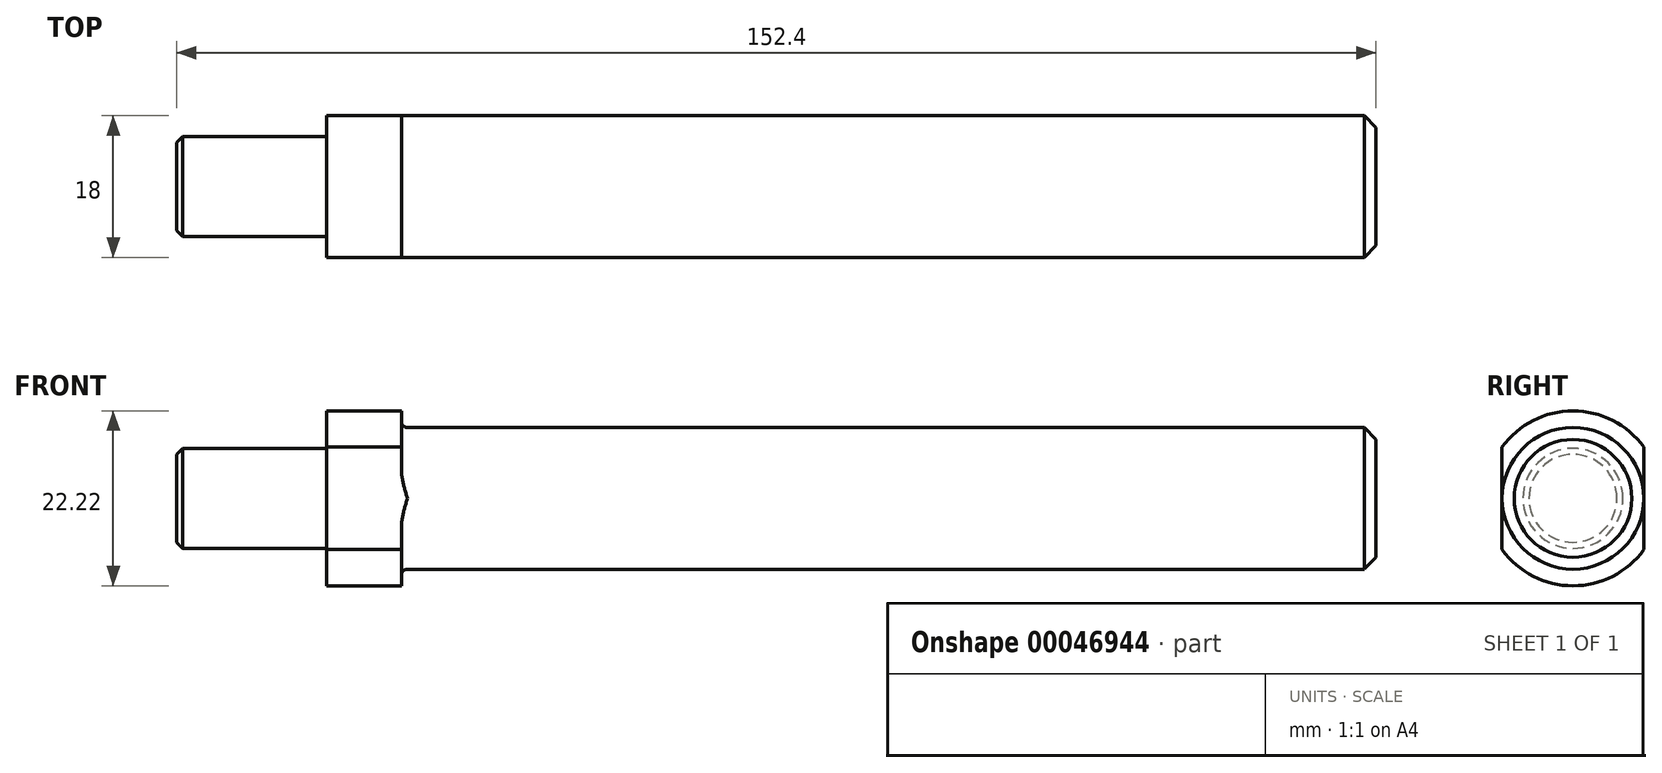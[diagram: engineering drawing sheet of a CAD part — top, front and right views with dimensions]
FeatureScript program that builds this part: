
annotation { "Feature Type Name" : "Feature", "Feature Type Description" : "" }
export const myFeature = defineFeature(function(context is Context, id is Id, definition is map)
    precondition{}
    {
        {
            var Q0;
            Q0=qCreatedBy(makeId("Right.planeOp"),FACE);
            var sketch = newSketch(context, id + "F0", { "sketchPlane" : qUnion([Q0])});
            skCircle(sketch, "E0", {"center": v(0, 0) * mm, "radius": 6.35 * mm});
            skSolve(sketch);
        }
        {
            var Q0;
            Q0=qSketchRegion(id+"F0",true);
            extrude(context, id + "F1", {"entities" : qUnion([Q0]), "oppositeDirection" : true, "depth" : 19.05 * mm});
        }
        {
            var Q0;
            Q0=makeQuery(id+"F1.opExtrude","CAP_EDGE",EDGE,{"disambiguationData":[OSD([sQuery(id+"F0.wireOp",EDGE,"E0")])],"isStart":false});
            chamfer(context, id + "F2", {"entities" : qUnion([Q0]), "width" : 0.76 * mm, "tangentPropagation" : true});
        }
        {
            var Q0;
            Q0=qCreatedBy(makeId("Right.planeOp"),FACE);
            var sketch = newSketch(context, id + "F3", { "sketchPlane" : qUnion([Q0])});
            skCircle(sketch, "E1", {"center": v(0, 0) * mm, "radius": 9 * mm});
            skSolve(sketch);
        }
        {
            var Q0;
            Q0=makeQuery(id+"F3.imprint","IMPRINT",FACE,{"disambiguationData":[TD([[makeQuery(id+"F3.imprint","IMPRINT",EDGE,{"derivedFrom":sQuery(id+"F3.wireOp",EDGE,"E1")}),1.0]])]});
            extrude(context, id + "F4", {"entities" : qUnion([Q0]), "operationType" : NewBodyOperationType.ADD, "depth" : 133.35 * mm});
        }
        {
            var Q0;
            Q0=qCreatedBy(makeId("Right.planeOp"),FACE);
            var sketch = newSketch(context, id + "F5", { "sketchPlane" : qUnion([Q0])});
            skCircle(sketch, "E2", {"center": v(0, 0) * mm, "radius": 11.11 * mm});
            skSolve(sketch);
        }
        {
            var Q0;
            Q0=qSketchRegion(id+"F5",true);
            extrude(context, id + "F6", {"entities" : qUnion([Q0]), "operationType" : NewBodyOperationType.ADD, "depth" : 9.52 * mm});
        }
        {
            var Q0;
            Q0=makeQuery(id+"F6.boolean.opBoolean","INTERSECT",EDGE,{"derivedFrom":[makeQuery(id+"F4.opExtrude","SWEPT_FACE",FACE,{"disambiguationData":[OSD([sQuery(id+"F3.wireOp",EDGE,"E1")])]}),makeQuery(id+"F6.opExtrude","CAP_FACE",FACE,{"disambiguationData":[OSD([sQuery(id+"F5.wireOp",EDGE,"E2")])],"isStart":false})]});
            fillet(context, id + "F7", {"entities" : qUnion([Q0]), "radius" : 0.76 * mm, "tangentPropagation" : true, "allowEdgeOverflow" : false});
        }
        {
            var Q0;
            Q0=makeQuery(id+"F4.opExtrude","CAP_FACE",FACE,{"disambiguationData":[OSD([sQuery(id+"F3.wireOp",EDGE,"E1")])],"isStart":false});
            chamfer(context, id + "F8", {"entities" : qUnion([Q0]), "width" : 1.52 * mm, "tangentPropagation" : true});
        }
        {
            var Q0;
            Q0=qCreatedBy(makeId("Top.planeOp"),FACE);
            var sketch = newSketch(context, id + "F9", { "sketchPlane" : qUnion([Q0])});
            skLineSegment(sketch, "E3", {"start": v(10.29, 9) * mm, "end": v(36.58, 9) * mm, "construction": true});
            skLineSegment(sketch, "E4.bottom", {"start": v(10.29, 9) * mm, "end": v(-2.96, 9) * mm});
            skLineSegment(sketch, "E4.top", {"start": v(10.29, 13.67) * mm, "end": v(-2.96, 13.67) * mm});
            skLineSegment(sketch, "E4.left", {"start": v(10.29, 9) * mm, "end": v(10.29, 13.67) * mm});
            skLineSegment(sketch, "E4.right", {"start": v(-2.96, 9) * mm, "end": v(-2.96, 13.67) * mm});
            skLineSegment(sketch, "E5", {"start": v(-21.58, 0) * mm, "end": v(40.55, 0) * mm, "construction": true});
            skLineSegment(sketch, "E6.MirrorCS", {"start": v(10.29, -9) * mm, "end": v(-2.96, -9) * mm});
            skLineSegment(sketch, "E7.MirrorCS", {"start": v(10.29, -13.67) * mm, "end": v(-2.96, -13.67) * mm});
            skLineSegment(sketch, "E8.MirrorCS", {"start": v(10.29, -9) * mm, "end": v(10.29, -13.67) * mm});
            skLineSegment(sketch, "E9.MirrorCS", {"start": v(-2.96, -9) * mm, "end": v(-2.96, -13.67) * mm});
            skSolve(sketch);
        }
        {
            var Q0;
            Q0=qSketchRegion(id+"F9",true);
            extrude(context, id + "F10", {"entities" : qUnion([Q0]), "operationType" : NewBodyOperationType.REMOVE, "endBound" : BoundingType.THROUGH_ALL, "oppositeDirection" : true, "depth" : 25.4 * mm, "hasSecondDirection" : true, "secondDirectionBound" : SecondDirectionBoundingType.THROUGH_ALL, "secondDirectionOppositeDirection" : false, "secondDirectionDepth" : 25.4 * mm});
        }
    });
